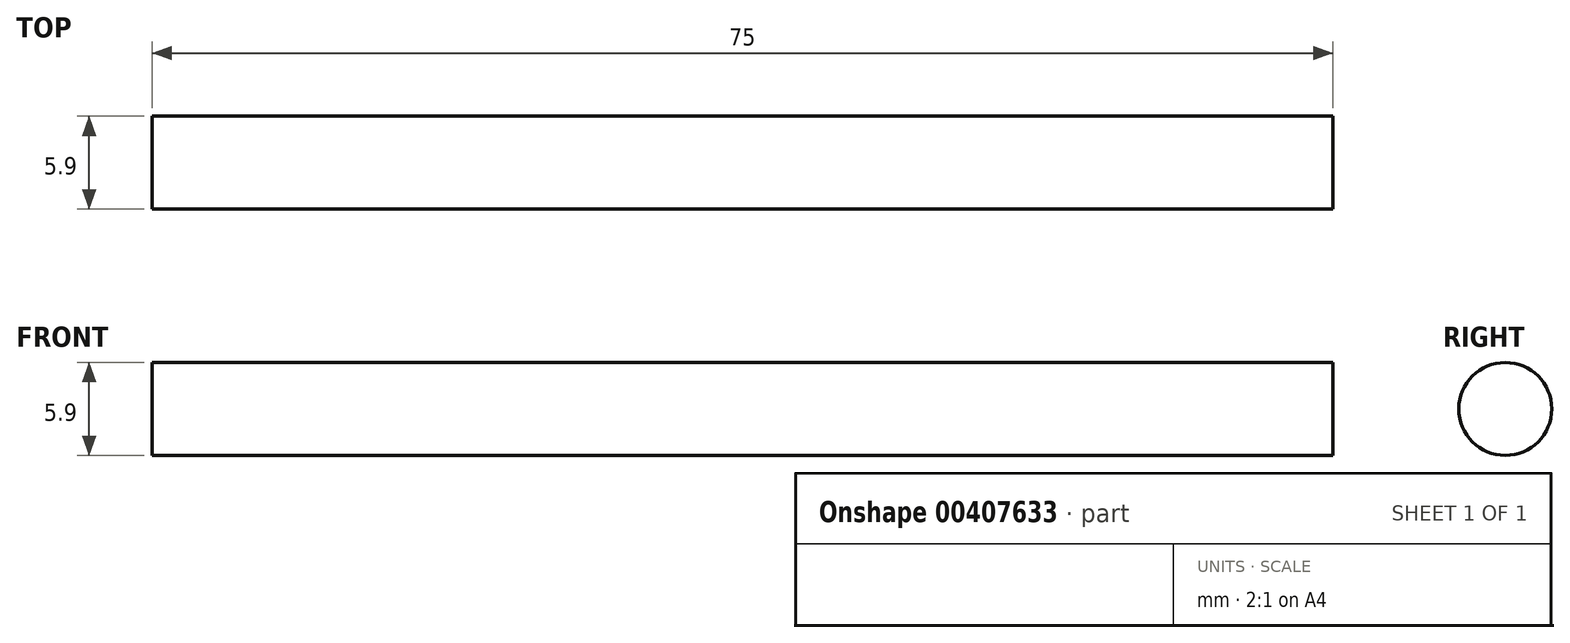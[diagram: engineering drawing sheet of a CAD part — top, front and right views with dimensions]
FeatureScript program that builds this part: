
annotation { "Feature Type Name" : "Feature", "Feature Type Description" : "" }
export const myFeature = defineFeature(function(context is Context, id is Id, definition is map)
    precondition{}
    {
        {
            var Q0;
            Q0=qCreatedBy(makeId("Right.planeOp"),FACE);
            var sketch = newSketch(context, id + "F0", { "sketchPlane" : qUnion([Q0])});
            skCircle(sketch, "E0", {"center": v(0, 0) * mm, "radius": 2.95 * mm});
            skSolve(sketch);
        }
        {
            var Q0;
            Q0=makeQuery(id+"F0.imprint","IMPRINT",FACE,{"disambiguationData":[TD([[makeQuery(id+"F0.imprint","IMPRINT",EDGE,{"derivedFrom":sQuery(id+"F0.wireOp",EDGE,"E0")}),1.0]])]});
            extrude(context, id + "F1", {"entities" : qUnion([Q0]), "depth" : 75 * mm});
        }
    });
